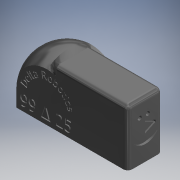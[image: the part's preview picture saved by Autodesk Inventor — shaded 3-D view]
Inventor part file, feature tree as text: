
AUTODESK INVENTOR PART (.ipt)
format: ipt  version: 2019 (Build 230136000, 136)  size: 1,036,288 bytes
history: native  units: mm (DEFAULTED — no unit token found)
features: extrude x17, sketch x15, plane x3, other x2, mirror x1, revolve x1, loft x1, fillet x1, projected_geometry x1
ambient origin geometry x8: Origin, YZ Plane, XZ Plane, XY Plane, X Axis, Y Axis, Z Axis, Center Point
bodies: Solid1 (feature_tree)
feature tree (42):
  extrude  "Extrusion1"  Depth=88.9mm
  extrude  "Extrusion2"  Depth=25.4mm
  extrude  "Extrusion3"  Depth=3.175mm TaperAngle=0.0deg
  plane  "Work Plane1"
  mirror  "Mirror1"
  plane  "Work Plane2"
  revolve  "Revolution1"  [1 undecoded]
  extrude  "Extrusion5"  Depth=44.45mm
  extrude  "Extrusion8"  TaperAngle=90.0deg  [1 undecoded]
  extrude  "Extrusion9"  Depth=38.1mm
  extrude  "Extrusion10"  Depth=1.5875mm TaperAngle=0.0deg
  extrude  "Extrusion11"  Depth=3.175mm
  extrude  "Extrusion12"  Depth=19.05mm
  extrude  "Extrusion13"  Depth=12.7mm
  extrude  "Extrusion14"  Depth=71.628mm
  extrude  "Extrusion16"  Depth=16.51mm TaperAngle=0.0deg
  extrude  "Extrusion17"  Depth=3.048mm
  plane  "Work Plane6"
  extrude  "Extrusion20"  Depth=6.35mm
  extrude  "Extrusion21"  Depth=6.35mm
  extrude  "Extrusion23"  Depth=6.35mm
  extrude  "Extrusion24"  Depth=6.35mm
  loft  "Loft4"
  fillet  "Fillet4"  Radius=55.88mm
  sketch  "Sketch1"  dims[d0=82.55mm d1=88.9mm]
  sketch  "Sketch2"  dims[d2=25.4mm d3=25.4mm]
  sketch  "Sketch3"  dims[d4=59.69mm d5=0.0mm d6=3.175mm d7=0.0mm]
  sketch  "Sketch5"  dims[d8=12.7mm d9=25.4mm]
  sketch  "Sketch8"  dims[d10=9.525mm d11=0.0mm d12=44.45mm]
  sketch  "Sketch10"  dims[d13=44.45mm d14=90.0deg]
  sketch  "Sketch11"  dims[d23=2.54mm d24=0.0mm d33=38.1mm]
  sketch  "Sketch15"  dims[d34=1.27mm d35=0.0mm d36=1.5875mm d37=0.0mm]
  sketch  "Sketch16"  dims[d38=3.175mm d39=3.175mm]
  sketch  "Sketch21"  dims[d40=3.175mm d41=19.05mm]
  sketch  "Sketch22"  dims[d42=12.7mm d43=12.7mm]
  sketch  "Sketch25"  dims[d44=12.7mm d46=71.628mm]
  sketch  "Sketch26"  dims[d47=25.4mm d48=0.0mm d53=16.51mm d54=0.0mm]
  sketch  "Sketch28"  dims[d55=25.4mm d56=0.0mm d57=3.048mm]
  sketch  "Sketch29"  dims[d58=3.048mm d59=6.35mm d60=6.35mm d61=8.001mm d63=24.003mm d64=25.4mm d65=0.0mm d72=55.88mm d73=0.0mm d84=3.175mm d85=6.35mm d88=6.35mm d89=68.58mm d90=0.0mm d92=74.93mm d93=0.0mm d100=6.35mm d101=6.35mm d102=3.175mm d103=0.0mm d104=50.00625mm d105=0.0mm d109=10.16mm d110=5.08mm d111=0.0mm d112=5.08mm d113=0.0mm d114=0.0mm d115=90.0deg d116=0.0mm d117=90.0deg d118=6.35mm]
  other  "Edges6"
  other  "Edges7"
  projected_geometry  "Projected Loop1"
note: 2 required parameter values undecoded (feature->parameter linkage not recoverable at this tier; creation-order binding heuristic only, values carry confidence <= 0.55)